# Revit family: Lockin Lockers AU_Custom Sports Locker_R22
name_source: partatom
category: Furniture
units: mm (PartAtom-declared; Revit-internal decimal feet)

## family parameters
Always vertical = Yes
Cut with Voids When Loaded = No
OmniClass Number = 23.40.20.27
OmniClass Title = Storage Shelving
Render Appearance Source = Family Geometry
Room Calculation Point = No
Shared = Yes
Work Plane-Based = Yes

## types (4) — shared parameters
Base Height Control = 100 mm  [stored 0.328084 ft]
Body/Frame Material = Material - Melamine - Laminex or Polytec Finish
Description = Sports Locker
Desired Base Height = 100 mm  [stored 0.328084 ft]
Desired Height = 2100 mm  [stored 6.88976 ft]
Door Material = Material - Melamine - Laminex or Polytec Finish
Door Type = Lockin_Locker Door_Standard_R22 : Standard Door/Combination Lock
H Locker = 400 mm  [stored 1.31234 ft]
Height Control = 2100 mm  [stored 6.88976 ft]
Manufacturer = Lockin Lockers AU
Maximum Base Height = 100 mm  [stored 0.328084 ft]
Maximum Height = 2100 mm  [stored 6.88976 ft]
Minimum Base Height = 100 mm  [stored 0.328084 ft]
Minimum Height = 1900 mm  [stored 6.2336 ft]
Shoe Box Height = 350 mm  [stored 1.14829 ft]
TH Wall = 18 mm  [stored 0.0590551 ft]
URL = https://www.lockin.com.au
zero-valued in all types: Default Elevation

## per-type parameters (varying)
| type | Bench Seat | Depth Control | Desired Depth | Desired Width | Locker Door | Maximum Depth | Maximum Width | Minimum Depth | Minimum Width | Model | Nested Seat | Offset Seat Front | SP1 | SP2 | SP3 | SP4 | Width Control |
| Sports Locker (SP1) | No | 600 mm | 600 mm | 600 mm | Yes | 700 mm  [stored 2.29659 ft] | 700 mm  [stored 2.29659 ft] | 500 mm  [stored 1.64042 ft] | 500 mm  [stored 1.64042 ft] | SP1 | Yes | 50 mm  [stored 0.164042 ft] | Yes | No | No | No | 600 mm |
| Sports Locker (SP2) | No | 500 mm  [stored 1.64042 ft] | 500 mm  [stored 1.64042 ft] | 600 mm | Yes | 600 mm | 700 mm  [stored 2.29659 ft] | 400 mm  [stored 1.31234 ft] | 500 mm  [stored 1.64042 ft] | SP2 | Yes | 250 mm  [stored 0.82021 ft] | No | Yes | No | No | 600 mm |
| Sports Locker (SP3) | No | 500 mm  [stored 1.64042 ft] | 500 mm  [stored 1.64042 ft] | 600 mm | No | 600 mm | 700 mm  [stored 2.29659 ft] | 400 mm  [stored 1.31234 ft] | 500 mm  [stored 1.64042 ft] | SP3 | Yes | 250 mm  [stored 0.82021 ft] | No | No | Yes | No | 600 mm |
| Sports Locker (SP4) | Yes | 550 mm | 550 mm | 400 mm  [stored 1.31234 ft] | Yes | 600 mm | 600 mm | 400 mm  [stored 1.31234 ft] | 300 mm | SP4 | No | 50 mm  [stored 0.164042 ft] | No | No | No | Yes | 400 mm  [stored 1.31234 ft] |

note: [stored X ft] marks values corroborated as IEEE doubles in the binary element streams (Revit-internal decimal feet)

## geometry (parser evidence)
native form markers: Sweep x6
no freeform markers — native parametric forms only
